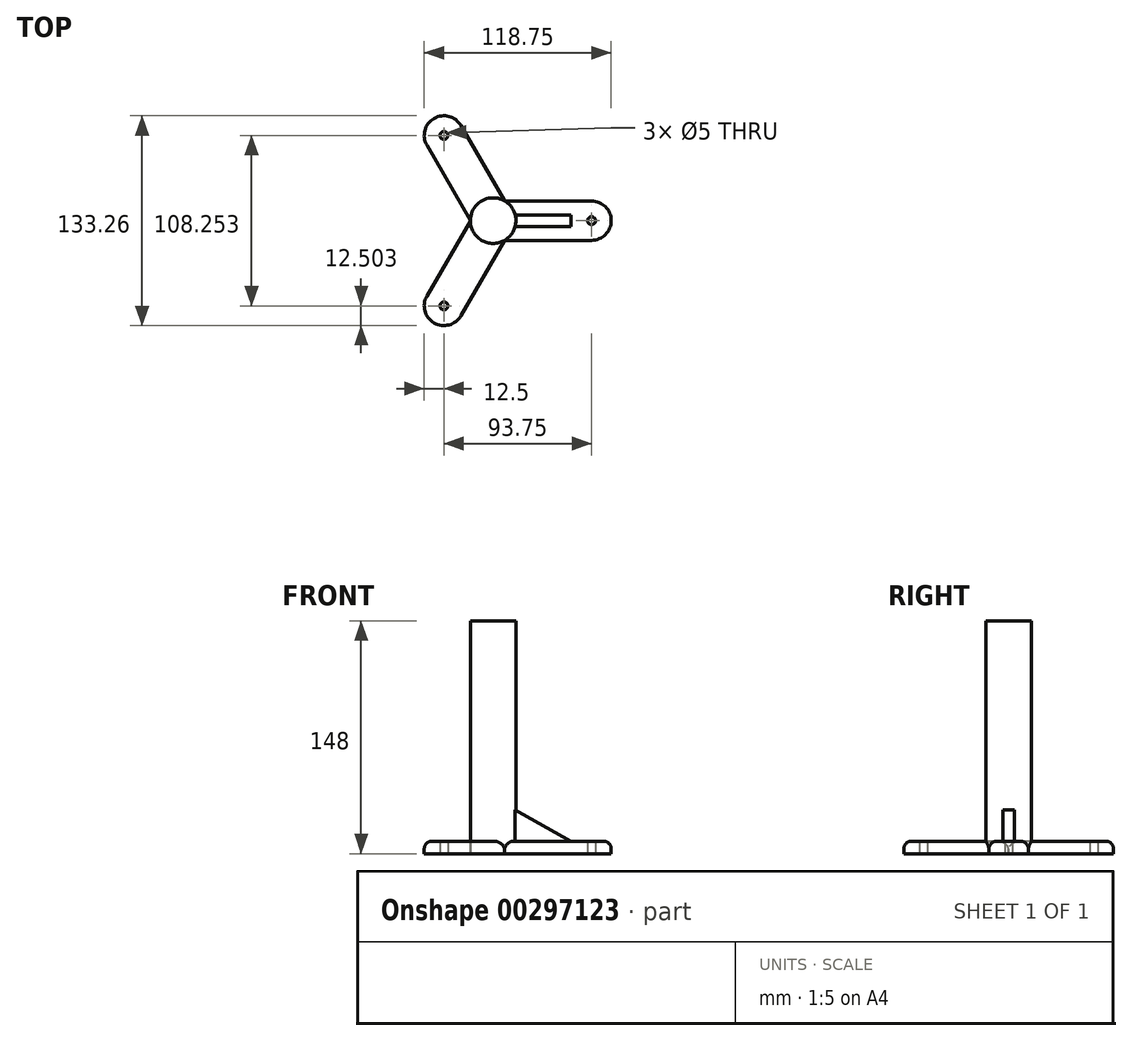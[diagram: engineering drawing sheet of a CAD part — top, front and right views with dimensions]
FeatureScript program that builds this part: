
annotation { "Feature Type Name" : "Feature", "Feature Type Description" : "" }
export const myFeature = defineFeature(function(context is Context, id is Id, definition is map)
    precondition{}
    {
        {
            var Q0;
            Q0=qCreatedBy(makeId("Top.planeOp"),FACE);
            var sketch = newSketch(context, id + "F0", { "sketchPlane" : qUnion([Q0])});
            skLineSegment(sketch, "E0.bottom", {"start": v(62.5, 12.5) * mm, "end": v(7.22, 12.5) * mm});
            skLineSegment(sketch, "E0.top", {"start": v(62.5, -12.5) * mm, "end": v(7.22, -12.5) * mm});
            skLineSegment(sketch, "E0.left", {"start": v(75, 0) * mm, "end": v(75, 0) * mm});
            skPoint(sketch, "E0.middle", {"position": v(0, 0) * mm});
            skPoint(sketch, "E0.right.start.orphan", {"position": v(-75, 12.5) * mm});
            skPoint(sketch, "E1.orphan", {"position": v(-75, -12.5) * mm});
            skPoint(sketch, "E2.visualSharp", {"position": v(75, 12.5) * mm});
            skArc(sketch, "E2.filletArc", {"start": v(75, 0) * mm, "mid": v(71.34, 8.84) * mm, "end": v(62.5, 12.5) * mm});
            skPoint(sketch, "E3.visualSharp", {"position": v(75, -12.5) * mm});
            skArc(sketch, "E3.filletArc", {"start": v(62.5, -12.5) * mm, "mid": v(71.34, -8.84) * mm, "end": v(75, 0) * mm});
            skCircle(sketch, "E4", {"center": v(62.5, 0) * mm, "radius": 2.5 * mm});
            skLineSegment(sketch, "E5.1.1", {"start": v(-42.08, 47.88) * mm, "end": v(-14.43, 0) * mm});
            skLineSegment(sketch, "E5.1.3", {"start": v(-20.42, 60.38) * mm, "end": v(7.22, 12.5) * mm});
            skArc(sketch, "E5.1.4", {"start": v(-20.42, 60.38) * mm, "mid": v(-28.01, 66.2) * mm, "end": v(-37.5, 64.95) * mm});
            skArc(sketch, "E5.1.5", {"start": v(-37.5, 64.95) * mm, "mid": v(-43.32, 57.36) * mm, "end": v(-42.08, 47.88) * mm});
            skLineSegment(sketch, "E5.2.1", {"start": v(-20.42, -60.38) * mm, "end": v(7.22, -12.5) * mm});
            skLineSegment(sketch, "E5.2.3", {"start": v(-42.08, -47.88) * mm, "end": v(-14.43, 0) * mm});
            skArc(sketch, "E5.2.4", {"start": v(-42.08, -47.88) * mm, "mid": v(-43.32, -57.36) * mm, "end": v(-37.5, -64.95) * mm});
            skArc(sketch, "E5.2.5", {"start": v(-37.5, -64.95) * mm, "mid": v(-28.01, -66.2) * mm, "end": v(-20.42, -60.38) * mm});
            skPoint(sketch, "E6.orphan", {"position": v(-10.83, 6.25) * mm});
            skPoint(sketch, "E7.orphan", {"position": v(-10.83, -6.25) * mm});
            skPoint(sketch, "E8.orphan", {"position": v(0, -12.5) * mm});
            skPoint(sketch, "E9.orphan", {"position": v(0, 12.5) * mm});
            skPoint(sketch, "E10.orphan", {"position": v(10.83, 6.25) * mm});
            skCircle(sketch, "E11", {"center": v(-31.25, 54.13) * mm, "radius": 2.5 * mm});
            skCircle(sketch, "E12", {"center": v(-31.25, -54.13) * mm, "radius": 2.5 * mm});
            skSolve(sketch);
        }
        {
            var Q0;
            Q0 = qSketchRegion(id + "F0", true);
            extrude(context, id + "F1", {"entities" : qUnion([Q0]), "depth" : 8 * mm});
        }
        {
            var Q0;
            Q0=makeQuery(id+"F1.opExtrude","CAP_EDGE",EDGE,{"disambiguationData":[OSD([sQuery(id+"F0.wireOp",EDGE,"E5.1.4"),sQuery(id+"F0.wireOp",EDGE,"E5.1.5")])],"isStart":false});
            var Q1;
            Q1=makeQuery(id+"F1.opExtrude","CAP_EDGE",EDGE,{"disambiguationData":[OSD([sQuery(id+"F0.wireOp",EDGE,"E5.2.3")])],"isStart":false});
            var Q2;
            Q2=makeQuery(id+"F1.opExtrude","CAP_EDGE",EDGE,{"disambiguationData":[OSD([sQuery(id+"F0.wireOp",EDGE,"E0.top")])],"isStart":false});
            fillet(context, id + "F2", {"entities" : qUnion([Q0, Q1, Q2]), "radius" : 5 * mm, "tangentPropagation" : true, "allowEdgeOverflow" : false});
        }
        {
            var Q0;
            Q0=makeQuery(id+"F1.opExtrude","CAP_FACE",FACE,{"disambiguationData":[OSD([sQuery(id+"F0.wireOp",EDGE,"E0.bottom"),sQuery(id+"F0.wireOp",EDGE,"E0.top"),sQuery(id+"F0.wireOp",EDGE,"E2.filletArc"),sQuery(id+"F0.wireOp",EDGE,"E3.filletArc"),sQuery(id+"F0.wireOp",EDGE,"E4"),sQuery(id+"F0.wireOp",EDGE,"E5.1.1"),sQuery(id+"F0.wireOp",EDGE,"E5.1.3"),sQuery(id+"F0.wireOp",EDGE,"E5.1.4"),sQuery(id+"F0.wireOp",EDGE,"E5.1.5"),sQuery(id+"F0.wireOp",EDGE,"E5.2.1"),sQuery(id+"F0.wireOp",EDGE,"E5.2.3"),sQuery(id+"F0.wireOp",EDGE,"E5.2.4"),sQuery(id+"F0.wireOp",EDGE,"E5.2.5"),sQuery(id+"F0.wireOp",EDGE,"E11"),sQuery(id+"F0.wireOp",EDGE,"E12")])],"isStart":false});
            var sketch = newSketch(context, id + "F3", { "sketchPlane" : qUnion([Q0])});
            skCircle(sketch, "E13", {"center": v(0, 0) * mm, "radius": 14.5 * mm});
            skSolve(sketch);
        }
        {
            var Q0;
            Q0 = qSketchRegion(id + "F3", true);
            extrude(context, id + "F4", {"entities" : qUnion([Q0]), "operationType" : NewBodyOperationType.ADD, "depth" : 140 * mm});
        }
        {
            var Q0;
            {var subQ1=sQuery(id+"F0.wireOp",EDGE,"E0.top");var subQ2=sQuery(id+"F3.wireOp",EDGE,"E13");Q0=makeQuery(id+"F4.boolean.opBoolean","SPLIT",FACE,{"disambiguationData":[TD([makeQuery(id+"F2.opFillet","BLEND_FACE",FACE,{"disambiguationData":[OSD([subQ1])]})])],"derivedFrom":makeQuery(id+"F4.opExtrude","CAP_FACE",FACE,{"disambiguationData":[OSD([subQ2])],"isStart":true})});}
            var Q1;
            {var subQ1=sQuery(id+"F0.wireOp",EDGE,"E0.bottom");var subQ2=sQuery(id+"F3.wireOp",EDGE,"E13");Q1=makeQuery(id+"F4.boolean.opBoolean","SPLIT",FACE,{"disambiguationData":[TD([makeQuery(id+"F2.opFillet","BLEND_FACE",FACE,{"disambiguationData":[OSD([subQ1])]})])],"derivedFrom":makeQuery(id+"F4.opExtrude","CAP_FACE",FACE,{"disambiguationData":[OSD([subQ2])],"isStart":true})});}
            var Q2;
            {var subQ1=sQuery(id+"F0.wireOp",EDGE,"E5.1.1");var subQ2=sQuery(id+"F3.wireOp",EDGE,"E13");Q2=makeQuery(id+"F4.boolean.opBoolean","SPLIT",FACE,{"disambiguationData":[TD([makeQuery(id+"F2.opFillet","BLEND_FACE",FACE,{"disambiguationData":[OSD([subQ1])]})])],"derivedFrom":makeQuery(id+"F4.opExtrude","CAP_FACE",FACE,{"disambiguationData":[OSD([subQ2])],"isStart":true})});}
            extrude(context, id + "F5", {"entities" : qUnion([Q0, Q1, Q2]), "operationType" : NewBodyOperationType.ADD, "depth" : 8 * mm});
        }
        {
            var Q0;
            {var subQ0=sQuery(id+"F0.wireOp",EDGE,"E3.filletArc");var subQ1=sQuery(id+"F0.wireOp",EDGE,"E2.filletArc");var subQ3=sQuery(id+"F0.wireOp",EDGE,"E0.top");var subQ4=sQuery(id+"F0.wireOp",EDGE,"E4");var subQ5=sQuery(id+"F0.wireOp",EDGE,"E0.bottom");Q0=makeQuery(id+"F4.boolean.opBoolean","SPLIT",FACE,{"disambiguationData":[TD([makeQuery(id+"F1.opExtrude","SWEPT_FACE",FACE,{"disambiguationData":[OSD([subQ4])]})])],"derivedFrom":makeQuery(id+"F1.opExtrude","CAP_FACE",FACE,{"disambiguationData":[OSD([subQ5,subQ3,subQ1,subQ0,subQ4,sQuery(id+"F0.wireOp",EDGE,"E5.1.1"),sQuery(id+"F0.wireOp",EDGE,"E5.1.3"),sQuery(id+"F0.wireOp",EDGE,"E5.1.4"),sQuery(id+"F0.wireOp",EDGE,"E5.1.5"),sQuery(id+"F0.wireOp",EDGE,"E5.2.1"),sQuery(id+"F0.wireOp",EDGE,"E5.2.3"),sQuery(id+"F0.wireOp",EDGE,"E5.2.4"),sQuery(id+"F0.wireOp",EDGE,"E5.2.5"),sQuery(id+"F0.wireOp",EDGE,"E11"),sQuery(id+"F0.wireOp",EDGE,"E12")])],"isStart":false})});}
            var sketch = newSketch(context, id + "F6", { "sketchPlane" : qUnion([Q0])});
            skLineSegment(sketch, "E14.bottom", {"start": v(49.34, -3.68) * mm, "end": v(-20.34, -3.68) * mm});
            skLineSegment(sketch, "E14.top", {"start": v(49.34, 3.68) * mm, "end": v(-20.34, 3.68) * mm});
            skLineSegment(sketch, "E14.left", {"start": v(49.34, -3.68) * mm, "end": v(49.34, 3.68) * mm});
            skLineSegment(sketch, "E14.right", {"start": v(-20.34, -3.68) * mm, "end": v(-20.34, 3.68) * mm});
            skPoint(sketch, "E14.middle", {"position": v(14.5, 0) * mm});
            skLineSegment(sketch, "E15", {"start": v(14.02, 3.68) * mm, "end": v(14.02, -3.68) * mm});
            skSolve(sketch);
        }
        {
            var Q0;
            {var subQ0=sQuery(id+"F6.wireOp",EDGE,"E14.left");Q0=makeQuery(id+"F6.imprint","IMPRINT",FACE,{"disambiguationData":[TD([[makeQuery(id+"F6.imprint","IMPRINT",EDGE,{"derivedFrom":subQ0}),1.0]])]});}
            extrude(context, id + "F7", {"entities" : qUnion([Q0]), "operationType" : NewBodyOperationType.ADD, "depth" : 20 * mm});
        }
        {
            var Q0;
            Q0=makeQuery(id+"F7.opExtrude","SWEPT_FACE",FACE,{"disambiguationData":[OSD([sQuery(id+"F6.wireOp",EDGE,"E14.bottom")])]});
            var sketch = newSketch(context, id + "F8", { "sketchPlane" : qUnion([Q0])});
            skLineSegment(sketch, "E16", {"start": v(49.34, 8) * mm, "end": v(14.02, 28) * mm});
            skLineSegment(sketch, "E17", {"start": v(14.02, 28) * mm, "end": v(49.34, 28) * mm});
            skLineSegment(sketch, "E18", {"start": v(49.34, 28) * mm, "end": v(49.34, 8) * mm});
            skSolve(sketch);
        }
        {
            var Q0;
            Q0 = qSketchRegion(id + "F8", true);
            extrude(context, id + "F9", {"entities" : qUnion([Q0]), "operationType" : NewBodyOperationType.REMOVE, "oppositeDirection" : true, "depth" : 80.7 * mm});
        }
    });
